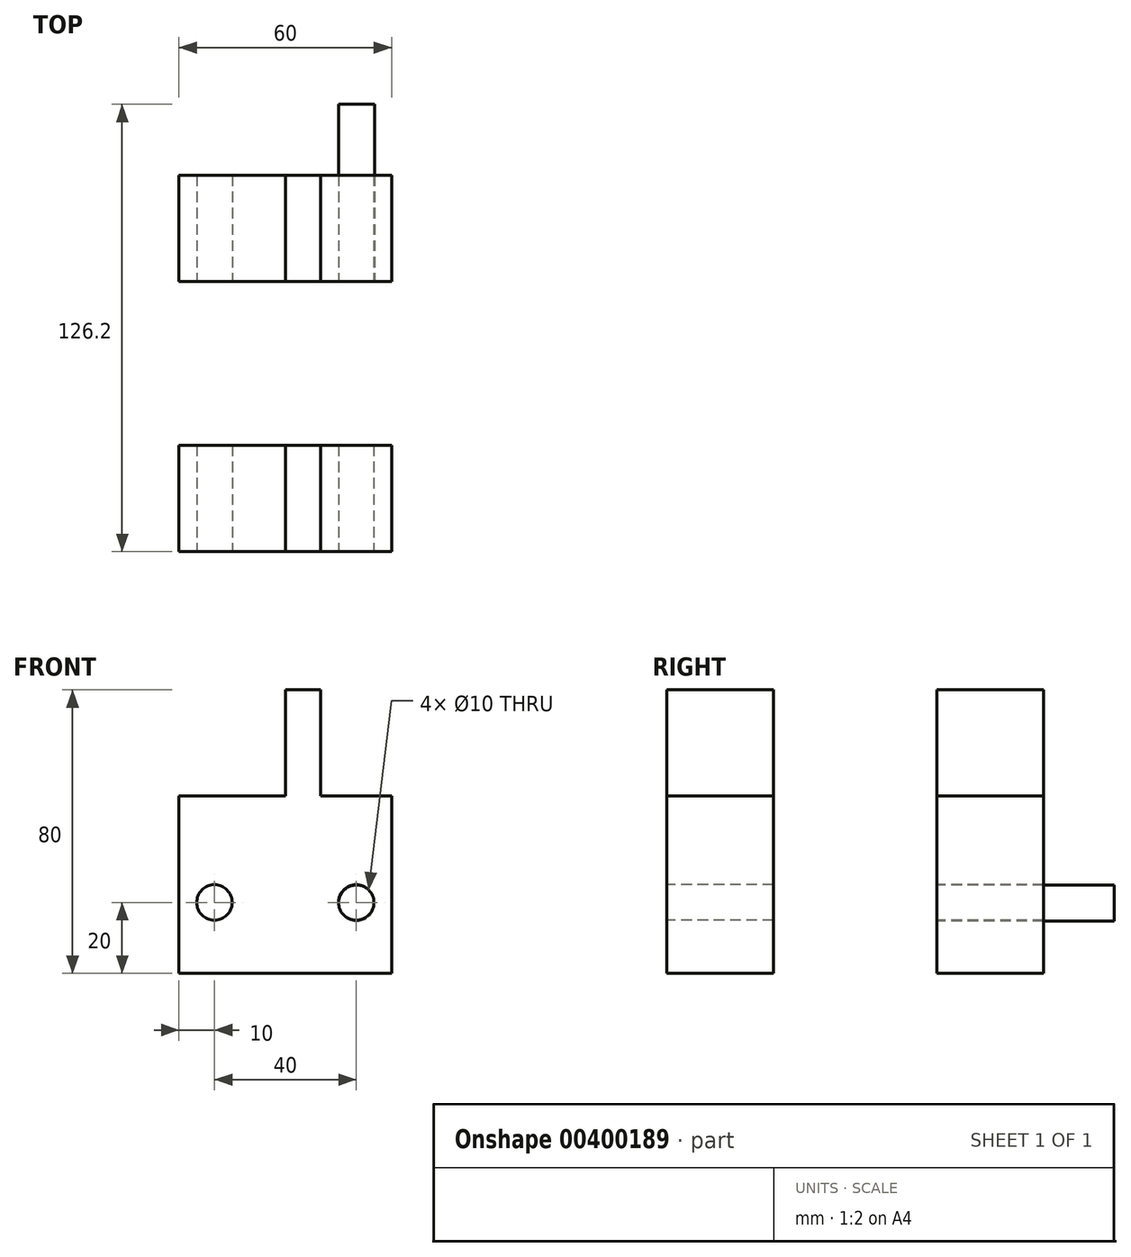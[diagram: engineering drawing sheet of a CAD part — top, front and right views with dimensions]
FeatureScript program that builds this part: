
annotation { "Feature Type Name" : "Feature", "Feature Type Description" : "" }
export const myFeature = defineFeature(function(context is Context, id is Id, definition is map)
    precondition{}
    {
        {
            var Q0;
            Q0=qCreatedBy(makeId("Front.planeOp"),FACE);
            var sketch = newSketch(context, id + "F0", { "sketchPlane" : qUnion([Q0])});
            skLineSegment(sketch, "E0.bottom", {"start": v(40, 47.84) * mm, "end": v(30, 47.84) * mm});
            skLineSegment(sketch, "E0.top", {"start": v(40, 80) * mm, "end": v(30, 80) * mm});
            skLineSegment(sketch, "E0.left", {"start": v(40, 47.84) * mm, "end": v(40, 80) * mm});
            skLineSegment(sketch, "E0.right", {"start": v(30, 47.84) * mm, "end": v(30, 80) * mm});
            skLineSegment(sketch, "E1", {"start": v(0, 0) * mm, "end": v(60, 0) * mm});
            skLineSegment(sketch, "E2", {"start": v(60, 0) * mm, "end": v(60, 0) * mm});
            skLineSegment(sketch, "E3", {"start": v(60, 50) * mm, "end": v(60, 0) * mm});
            skLineSegment(sketch, "E4", {"start": v(60, 50) * mm, "end": v(0, 50) * mm});
            skLineSegment(sketch, "E5", {"start": v(0, 50) * mm, "end": v(0, 50) * mm});
            skLineSegment(sketch, "E6", {"start": v(0, 0) * mm, "end": v(0, 50) * mm});
            skSolve(sketch);
        }
        {
            var Q0;
            {var subQ1=sQuery(id+"F0.wireOp",EDGE,"E0.bottom");Q0=makeQuery(id+"F0.imprint","IMPRINT",FACE,{"disambiguationData":[TD([[makeQuery(id+"F0.imprint","IMPRINT",EDGE,{"derivedFrom":subQ1}),1.0]])]});}
            var Q1;
            {var subQ0=sQuery(id+"F0.wireOp",EDGE,"E0.top");Q1=makeQuery(id+"F0.imprint","IMPRINT",FACE,{"disambiguationData":[TD([[makeQuery(id+"F0.imprint","IMPRINT",EDGE,{"derivedFrom":subQ0}),1.0]])]});}
            var Q2;
            {var subQ0=sQuery(id+"F0.wireOp",EDGE,"E0.bottom");Q2=makeQuery(id+"F0.imprint","IMPRINT",FACE,{"disambiguationData":[TD([[makeQuery(id+"F0.imprint","IMPRINT",EDGE,{"derivedFrom":subQ0}),-1.0]])]});}
            var Q3;
            Q3=sQuery(id+"F0.wireOp",EDGE,"E4");
            var Q4;
            Q4=sQuery(id+"F0.wireOp",EDGE,"E6");
            var Q5;
            Q5=sQuery(id+"F0.wireOp",EDGE,"E1");
            var Q6;
            Q6=sQuery(id+"F0.wireOp",EDGE,"E3");
            extrude(context, id + "F1", {"entities" : qUnion([Q0, Q1, Q2]), "surfaceEntities" : qUnion([Q3, Q4, Q5, Q6]), "depth" : 30 * mm});
        }
        {
            var Q0;
            Q0=makeQuery(id+"F1.opExtrude","CAP_FACE",FACE,{"disambiguationData":[OSD([sQuery(id+"F0.wireOp",EDGE,"E0.top"),sQuery(id+"F0.wireOp",EDGE,"E0.left"),sQuery(id+"F0.wireOp",EDGE,"E0.right"),sQuery(id+"F0.wireOp",EDGE,"E1"),sQuery(id+"F0.wireOp",EDGE,"E3"),sQuery(id+"F0.wireOp",EDGE,"E4"),sQuery(id+"F0.wireOp",EDGE,"E6")])],"isStart":false});
            var sketch = newSketch(context, id + "F2", { "sketchPlane" : qUnion([Q0])});
            skCircle(sketch, "E7", {"center": v(10, 20) * mm, "radius": 5 * mm});
            skLineSegment(sketch, "E8", {"start": v(30, 0) * mm, "end": v(30, 50) * mm, "construction": true});
            skCircle(sketch, "E9.MirrorC", {"center": v(50, 20) * mm, "radius": 5 * mm});
            skSolve(sketch);
        }
        {
            var Q0;
            Q0 = qSketchRegion(id + "F2", true);
            extrude(context, id + "F3", {"entities" : qUnion([Q0]), "operationType" : NewBodyOperationType.REMOVE, "endBound" : BoundingType.THROUGH_ALL, "oppositeDirection" : true, "depth" : 25.4 * mm});
        }
        {
            var Q0;
            Q0=makeQuery(id+"F1.opExtrude","SWEPT_BODY",BODY,{"disambiguationData":[OSD([sQuery(id+"F0.wireOp",EDGE,"E0.top"),sQuery(id+"F0.wireOp",EDGE,"E0.left"),sQuery(id+"F0.wireOp",EDGE,"E0.right"),sQuery(id+"F0.wireOp",EDGE,"E1"),sQuery(id+"F0.wireOp",EDGE,"E3"),sQuery(id+"F0.wireOp",EDGE,"E4"),sQuery(id+"F0.wireOp",EDGE,"E6")])]});
            var Q1;
            Q1=makeQuery(id+"F1.opExtrude","SWEPT_EDGE",EDGE,{"disambiguationData":[OSD([sQuery(id+"F0.wireOp",EDGE,"E3"),sQuery(id+"F0.wireOp",EDGE,"E4")])]});
            transform(context, id + "F4", {"entities" : qUnion([Q0]), "transformType" : TransformType.TRANSLATION_DISTANCE, "transformDirection" : qUnion([Q1]), "distance" : 76.2 * mm, "oppositeDirection" : true, "makeCopy" : true});
        }
        {
            var Q0;
            Q0=makeQuery(id+"F1.opExtrude","CAP_FACE",FACE,{"disambiguationData":[OSD([sQuery(id+"F0.wireOp",EDGE,"E0.top"),sQuery(id+"F0.wireOp",EDGE,"E0.left"),sQuery(id+"F0.wireOp",EDGE,"E0.right"),sQuery(id+"F0.wireOp",EDGE,"E1"),sQuery(id+"F0.wireOp",EDGE,"E3"),sQuery(id+"F0.wireOp",EDGE,"E4"),sQuery(id+"F0.wireOp",EDGE,"E6")])],"isStart":false});
            var sketch = newSketch(context, id + "F5", { "sketchPlane" : qUnion([Q0])});
            skCircle(sketch, "E10", {"center": v(50.09, 19.83) * mm, "radius": 5.1 * mm});
            skPoint(sketch, "E10.first.point", {"position": v(45, 20.02) * mm});
            skPoint(sketch, "E10.second.point", {"position": v(52.98, 24.02) * mm});
            skPoint(sketch, "E10.third.point", {"position": v(53.35, 15.92) * mm});
            skSolve(sketch);
        }
        {
            var Q0;
            Q0 = qSketchRegion(id + "F5", true);
            extrude(context, id + "F6", {"entities" : qUnion([Q0]), "oppositeDirection" : true, "depth" : 50 * mm});
        }
    });
